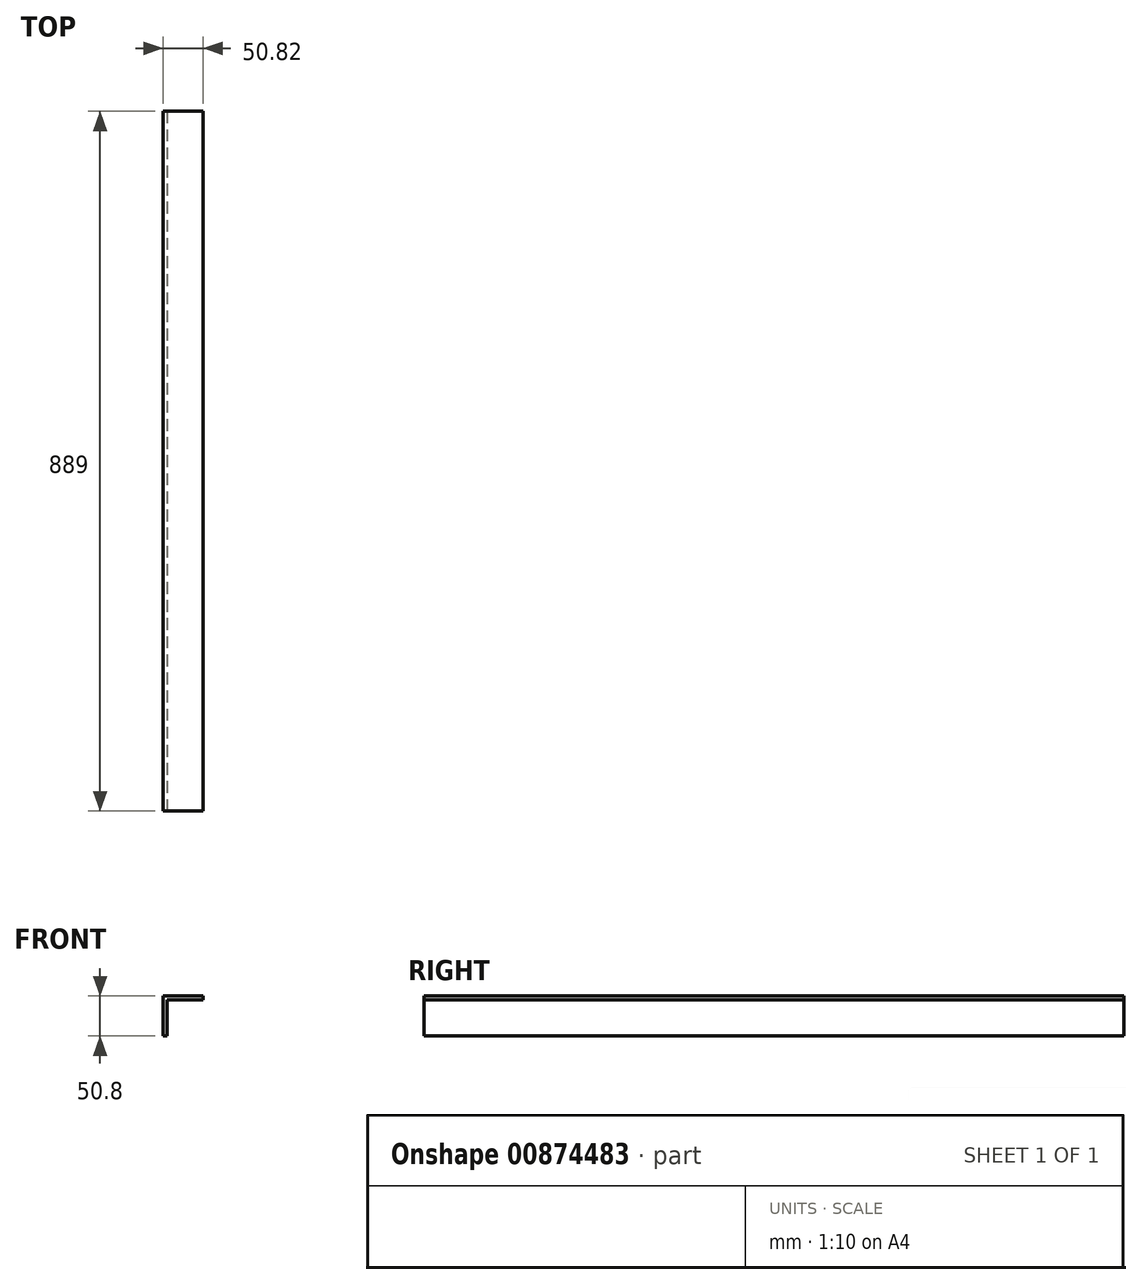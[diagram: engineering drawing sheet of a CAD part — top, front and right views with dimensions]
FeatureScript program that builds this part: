
annotation { "Feature Type Name" : "Feature", "Feature Type Description" : "" }
export const myFeature = defineFeature(function(context is Context, id is Id, definition is map)
    precondition{}
    {
        {
            var Q0;
            Q0=qCreatedBy(makeId("Front.planeOp"),FACE);
            var sketch = newSketch(context, id + "F0", { "sketchPlane" : qUnion([Q0])});
            skLineSegment(sketch, "E0.left", {"start": v(-50.8, 21.83) * mm, "end": v(-50.82, -28.97) * mm});
            skPoint(sketch, "E0.middle", {"position": v(0, 0) * mm});
            skLineSegment(sketch, "E1", {"start": v(-46.06, -28.97) * mm, "end": v(-46.06, 17.07) * mm});
            skLineSegment(sketch, "E2", {"start": v(-50.82, -28.97) * mm, "end": v(-46.06, -28.97) * mm});
            skLineSegment(sketch, "E3", {"start": v(-50.8, 21.83) * mm, "end": v(0, 21.8) * mm});
            skLineSegment(sketch, "E4", {"start": v(0, 21.8) * mm, "end": v(0, 17.07) * mm});
            skLineSegment(sketch, "E5", {"start": v(-46.06, 17.07) * mm, "end": v(0, 17.07) * mm});
            skSolve(sketch);
        }
        {
            var Q0;
            Q0=qSketchRegion(id+"F0",true);
            extrude(context, id + "F1", {"entities" : qUnion([Q0]), "oppositeDirection" : true, "depth" : 889 * mm, "offsetDistance" : 25.4 * mm});
        }
    });
